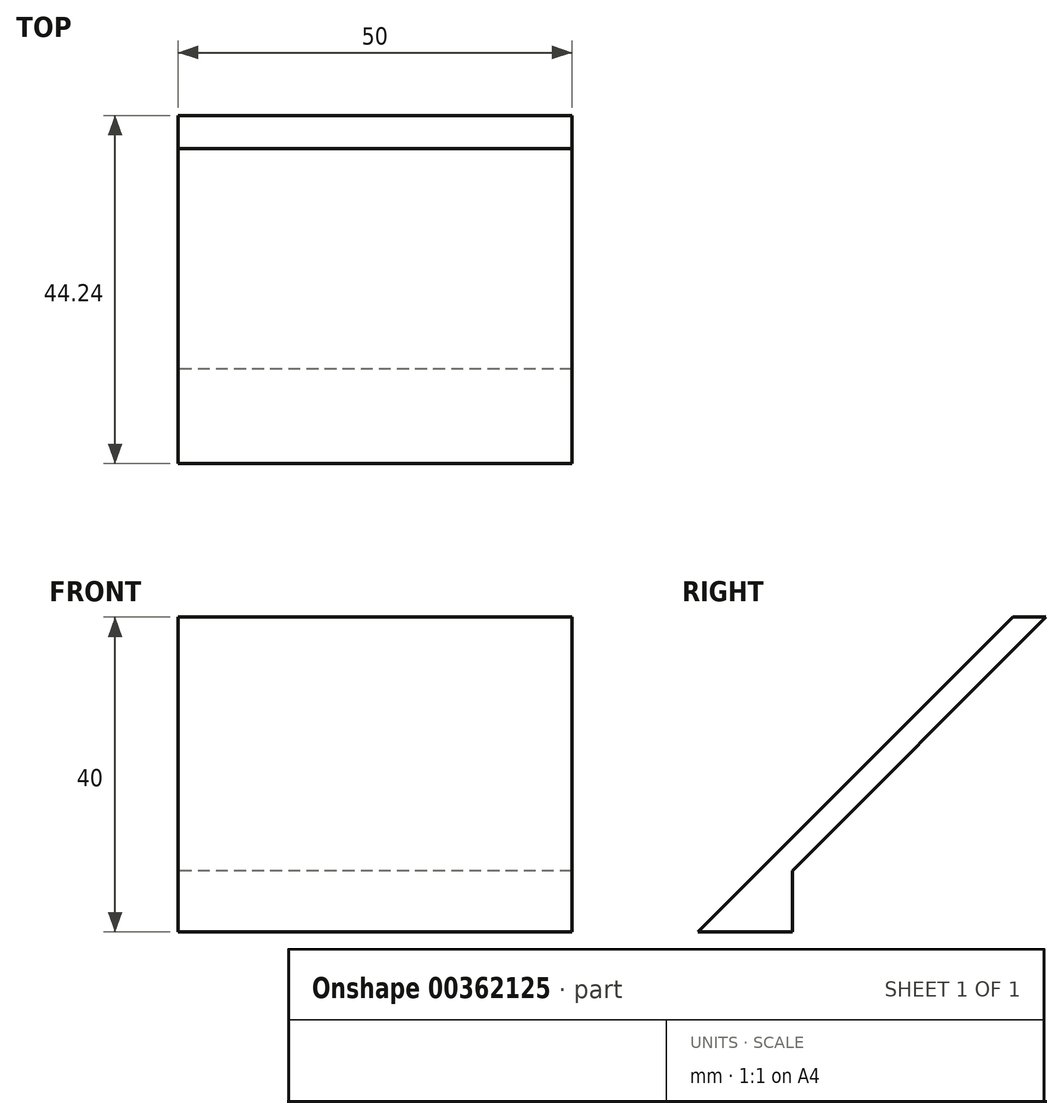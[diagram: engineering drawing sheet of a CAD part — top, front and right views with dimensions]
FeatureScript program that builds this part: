
annotation { "Feature Type Name" : "Feature", "Feature Type Description" : "" }
export const myFeature = defineFeature(function(context is Context, id is Id, definition is map)
    precondition{}
    {
        {
            var Q0;
            Q0=qCreatedBy(makeId("Right.planeOp"),FACE);
            var sketch = newSketch(context, id + "F0", { "sketchPlane" : qUnion([Q0])});
            skLineSegment(sketch, "E0", {"start": v(0, 0) * mm, "end": v(40, 40) * mm});
            skLineSegment(sketch, "E1", {"start": v(40, 40) * mm, "end": v(44.24, 40) * mm});
            skLineSegment(sketch, "E2", {"start": v(44.24, 40) * mm, "end": v(4.24, 0) * mm});
            skLineSegment(sketch, "E3", {"start": v(4.24, 0) * mm, "end": v(0, 0) * mm});
            skLineSegment(sketch, "E4", {"start": v(12, 0) * mm, "end": v(12, 7.76) * mm});
            skLineSegment(sketch, "E5", {"start": v(12, 0) * mm, "end": v(4.24, 0) * mm});
            skSolve(sketch);
        }
        {
            var Q0;
            Q0=makeQuery(id+"F0.imprint","IMPRINT",FACE,{"disambiguationData":[TD([[makeQuery(id+"F0.imprint","IMPRINT",EDGE,{"derivedFrom":sQuery(id+"F0.wireOp",EDGE,"E0")}),-1.0]])]});
            var Q1;
            {var subQ2=sQuery(id+"F0.wireOp",EDGE,"E4");Q1=makeQuery(id+"F0.imprint","IMPRINT",FACE,{"disambiguationData":[TD([[makeQuery(id+"F0.imprint","IMPRINT",EDGE,{"derivedFrom":subQ2}),1.0]])]});}
            extrude(context, id + "F1", {"entities" : qUnion([Q0, Q1]), "depth" : 50 * mm, "offsetDistance" : 25 * mm});
        }
    });
